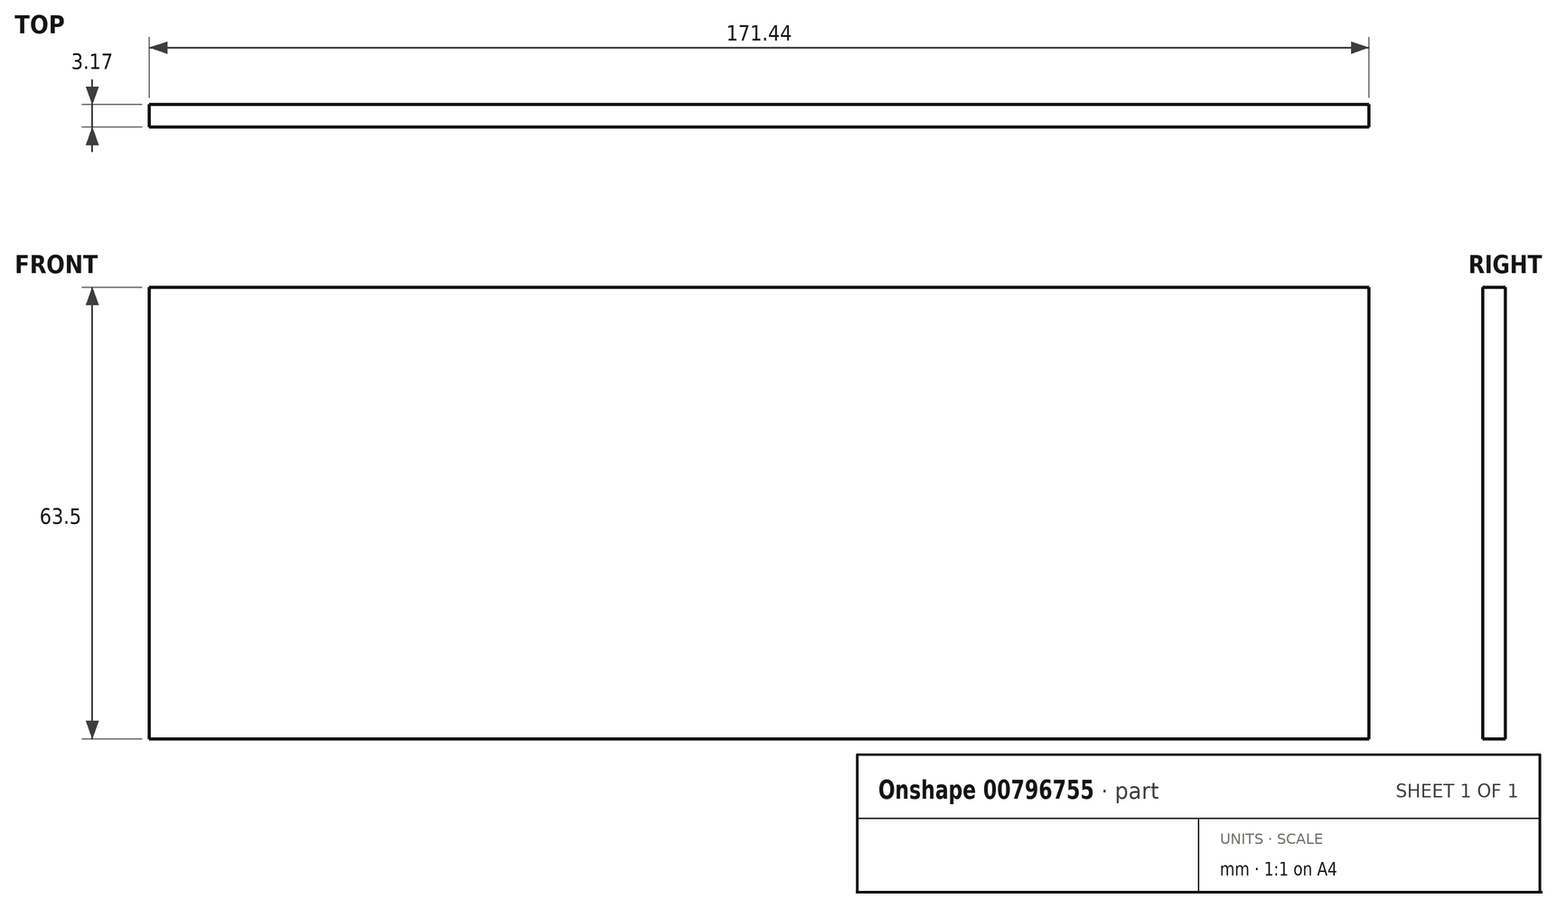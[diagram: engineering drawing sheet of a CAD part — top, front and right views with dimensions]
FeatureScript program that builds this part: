
annotation { "Feature Type Name" : "Feature", "Feature Type Description" : "" }
export const myFeature = defineFeature(function(context is Context, id is Id, definition is map)
    precondition{}
    {
        {
            var Q0;
            Q0=qCreatedBy(makeId("Front.planeOp"),FACE);
            var sketch = newSketch(context, id + "F0", { "sketchPlane" : qUnion([Q0])});
            skLineSegment(sketch, "E0.bottom", {"start": v(85.73, 31.75) * mm, "end": v(-85.72, 31.75) * mm});
            skLineSegment(sketch, "E0.top", {"start": v(85.72, -31.75) * mm, "end": v(-85.73, -31.75) * mm});
            skLineSegment(sketch, "E0.left", {"start": v(85.73, 31.75) * mm, "end": v(85.72, -31.75) * mm});
            skLineSegment(sketch, "E0.right", {"start": v(-85.72, 31.75) * mm, "end": v(-85.73, -31.75) * mm});
            skPoint(sketch, "E0.middle", {"position": v(0, 0) * mm});
            skSolve(sketch);
        }
        {
            var Q0;
            Q0=qSketchRegion(id+"F0",true);
            extrude(context, id + "F1", {"entities" : qUnion([Q0]), "depth" : 3.17 * mm, "offsetDistance" : 25.4 * mm});
        }
    });
